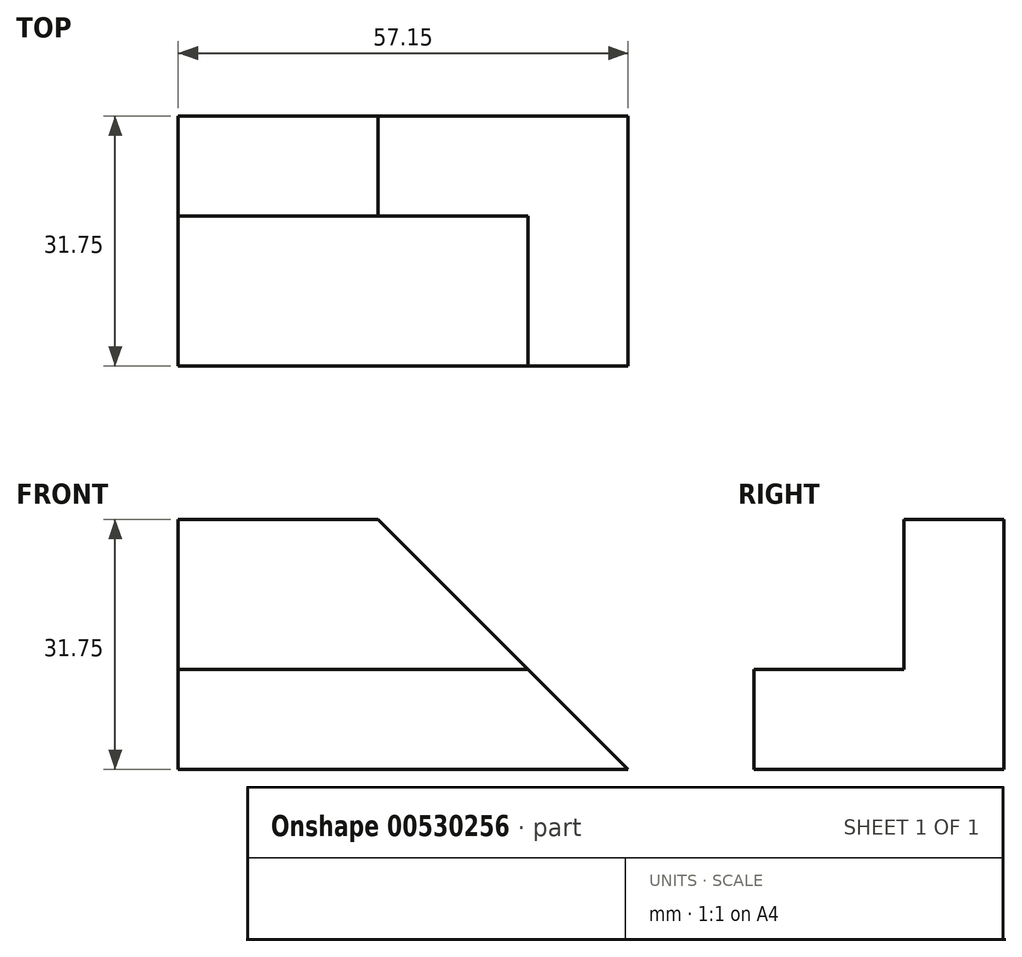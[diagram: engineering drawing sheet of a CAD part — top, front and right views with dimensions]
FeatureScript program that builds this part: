
annotation { "Feature Type Name" : "Feature", "Feature Type Description" : "" }
export const myFeature = defineFeature(function(context is Context, id is Id, definition is map)
    precondition{}
    {
        {
            var Q0;
            Q0=qCreatedBy(makeId("Front.planeOp"),FACE);
            var sketch = newSketch(context, id + "F0", { "sketchPlane" : qUnion([Q0])});
            skLineSegment(sketch, "E0", {"start": v(-83.06, 0) * mm, "end": v(-25.9, 0) * mm});
            skLineSegment(sketch, "E1", {"start": v(-25.9, 0) * mm, "end": v(-25.9, 12.7) * mm});
            skLineSegment(sketch, "E2", {"start": v(-25.9, 12.7) * mm, "end": v(-83.06, 12.7) * mm});
            skLineSegment(sketch, "E3", {"start": v(-83.06, 12.7) * mm, "end": v(-83.06, 0) * mm});
            skSolve(sketch);
        }
        {
            var Q0;
            Q0 = qSketchRegion(id + "F0", true);
            extrude(context, id + "F1", {"entities" : qUnion([Q0]), "depth" : 31.75 * mm, "offsetDistance" : 25.4 * mm});
        }
        {
            var Q0;
            Q0=makeQuery(id+"F1.opExtrude","CAP_FACE",FACE,{"disambiguationData":[OSD([sQuery(id+"F0.wireOp",EDGE,"E0"),sQuery(id+"F0.wireOp",EDGE,"E1"),sQuery(id+"F0.wireOp",EDGE,"E2"),sQuery(id+"F0.wireOp",EDGE,"E3")])],"isStart":true});
            var sketch = newSketch(context, id + "F2", { "sketchPlane" : qUnion([Q0])});
            skLineSegment(sketch, "E4", {"start": v(25.9, 12.7) * mm, "end": v(25.9, 31.75) * mm});
            skLineSegment(sketch, "E5", {"start": v(25.9, 31.75) * mm, "end": v(83.06, 31.75) * mm});
            skLineSegment(sketch, "E6", {"start": v(83.06, 31.75) * mm, "end": v(83.06, 12.7) * mm});
            skLineSegment(sketch, "E7", {"start": v(83.06, 12.7) * mm, "end": v(25.9, 12.7) * mm});
            skSolve(sketch);
        }
        {
            var Q0;
            Q0 = qSketchRegion(id + "F2", true);
            extrude(context, id + "F3", {"entities" : qUnion([Q0]), "operationType" : NewBodyOperationType.ADD, "oppositeDirection" : true, "depth" : 12.7 * mm, "offsetDistance" : 25.4 * mm});
        }
        {
            var Q0;
            Q0=makeQuery(id+"F1.opExtrude","CAP_FACE",FACE,{"disambiguationData":[OSD([sQuery(id+"F0.wireOp",EDGE,"E0"),sQuery(id+"F0.wireOp",EDGE,"E1"),sQuery(id+"F0.wireOp",EDGE,"E2"),sQuery(id+"F0.wireOp",EDGE,"E3")])],"isStart":false});
            var sketch = newSketch(context, id + "F4", { "sketchPlane" : qUnion([Q0])});
            skLineSegment(sketch, "E8", {"start": v(-25.9, 0) * mm, "end": v(-57.66, 31.75) * mm});
            skLineSegment(sketch, "E9", {"start": v(-57.66, 31.75) * mm, "end": v(-25.9, 31.75) * mm});
            skLineSegment(sketch, "E10", {"start": v(-25.9, 31.75) * mm, "end": v(-25.9, 0) * mm});
            skSolve(sketch);
        }
        {
            var Q0;
            Q0 = qSketchRegion(id + "F4", true);
            extrude(context, id + "F5", {"entities" : qUnion([Q0]), "operationType" : NewBodyOperationType.REMOVE, "endBound" : BoundingType.THROUGH_ALL, "oppositeDirection" : true, "depth" : 25.4 * mm, "offsetDistance" : 25.4 * mm});
        }
    });
